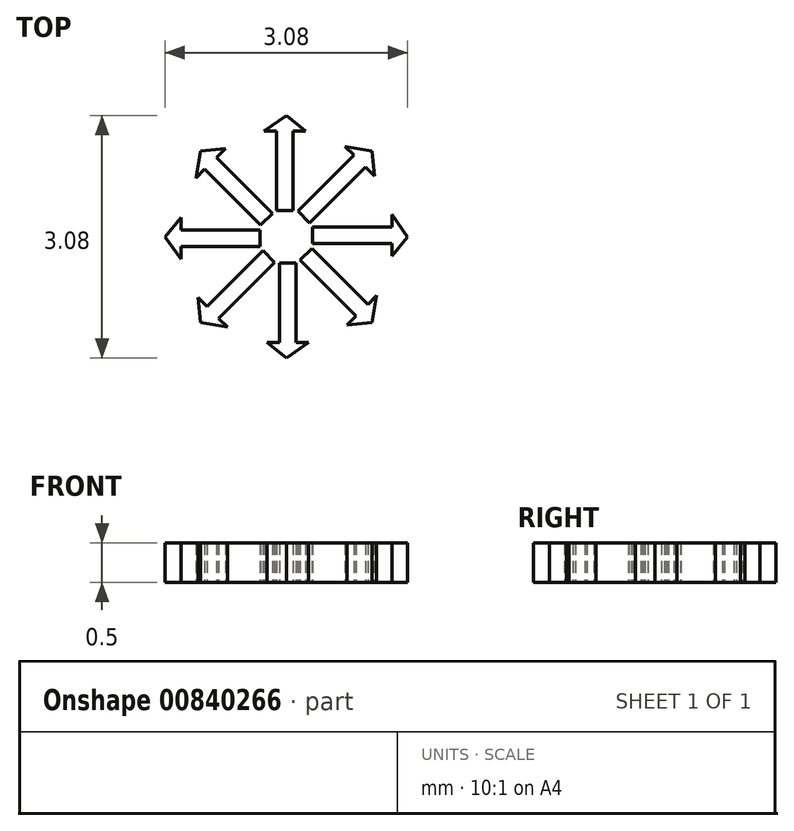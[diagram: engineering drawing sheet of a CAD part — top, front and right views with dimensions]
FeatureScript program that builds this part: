
annotation { "Feature Type Name" : "Feature", "Feature Type Description" : "" }
export const myFeature = defineFeature(function(context is Context, id is Id, definition is map)
    precondition{}
    {
        {
            var Q0;
            Q0=qCreatedBy(makeId("Top.planeOp"),FACE);
            var sketch = newSketch(context, id + "F0", { "sketchPlane" : qUnion([Q0])});
            skLineSegment(sketch, "E0.2.5", {"start": v(-1.34, -0.04) * mm, "end": v(-1.34, -0.15) * mm});
            skLineSegment(sketch, "E0.2.6", {"start": v(-0.34, -0.04) * mm, "end": v(-0.34, 0.04) * mm});
            skLineSegment(sketch, "E0.2.7", {"start": v(-1.34, 0.04) * mm, "end": v(-1.34, 0.15) * mm});
            skLineSegment(sketch, "E0.2.8", {"start": v(-1.34, -0.04) * mm, "end": v(-1.34, 0.04) * mm});
            skLineSegment(sketch, "E1.0", {"start": v(-1.34, 0.09) * mm, "end": v(-0.34, 0.09) * mm});
            skLineSegment(sketch, "E2.0", {"start": v(-1.34, -0.13) * mm, "end": v(-0.34, -0.13) * mm});
            skLineSegment(sketch, "E3", {"start": v(-0.34, 0.09) * mm, "end": v(-0.34, -0.13) * mm});
            skLineSegment(sketch, "E4", {"start": v(-1.34, 0.09) * mm, "end": v(-1.34, 0.25) * mm});
            skLineSegment(sketch, "E5", {"start": v(-1.34, -0.13) * mm, "end": v(-1.34, -0.29) * mm});
            skLineSegment(sketch, "E6", {"start": v(-1.34, 0.25) * mm, "end": v(-1.54, 0) * mm});
            skLineSegment(sketch, "E7", {"start": v(-1.34, -0.29) * mm, "end": v(-1.54, 0) * mm});
            skLineSegment(sketch, "E8.1.0", {"start": v(-1.12, -0.77) * mm, "end": v(-1.09, -1.09) * mm});
            skLineSegment(sketch, "E8.1.1", {"start": v(-1, -0.89) * mm, "end": v(-0.3, -0.18) * mm});
            skLineSegment(sketch, "E8.1.2", {"start": v(-0.75, -1.15) * mm, "end": v(-1.09, -1.09) * mm});
            skLineSegment(sketch, "E8.1.3", {"start": v(-0.86, -1.04) * mm, "end": v(-0.15, -0.33) * mm});
            skLineSegment(sketch, "E8.1.4", {"start": v(-1, -0.89) * mm, "end": v(-1.12, -0.77) * mm});
            skLineSegment(sketch, "E8.1.5", {"start": v(-0.86, -1.04) * mm, "end": v(-0.75, -1.15) * mm});
            skLineSegment(sketch, "E8.1.6", {"start": v(-0.21, -0.26) * mm, "end": v(-0.26, -0.21) * mm});
            skLineSegment(sketch, "E8.1.7", {"start": v(-0.3, -0.18) * mm, "end": v(-0.15, -0.33) * mm});
            skLineSegment(sketch, "E8.1.8", {"start": v(-0.92, -0.97) * mm, "end": v(-0.84, -1.05) * mm});
            skLineSegment(sketch, "E8.1.9", {"start": v(-0.92, -0.97) * mm, "end": v(-0.97, -0.92) * mm});
            skLineSegment(sketch, "E8.1.10", {"start": v(-0.97, -0.92) * mm, "end": v(-1.05, -0.84) * mm});
            skLineSegment(sketch, "E8.2.0", {"start": v(-0.25, -1.34) * mm, "end": v(0, -1.54) * mm});
            skLineSegment(sketch, "E8.2.1", {"start": v(-0.09, -1.34) * mm, "end": v(-0.09, -0.34) * mm});
            skLineSegment(sketch, "E8.2.2", {"start": v(0.29, -1.34) * mm, "end": v(0, -1.54) * mm});
            skLineSegment(sketch, "E8.2.3", {"start": v(0.13, -1.34) * mm, "end": v(0.13, -0.34) * mm});
            skLineSegment(sketch, "E8.2.4", {"start": v(-0.09, -1.34) * mm, "end": v(-0.25, -1.34) * mm});
            skLineSegment(sketch, "E8.2.5", {"start": v(0.13, -1.34) * mm, "end": v(0.29, -1.34) * mm});
            skLineSegment(sketch, "E8.2.6", {"start": v(0.04, -0.34) * mm, "end": v(-0.04, -0.34) * mm});
            skLineSegment(sketch, "E8.2.7", {"start": v(-0.09, -0.34) * mm, "end": v(0.13, -0.34) * mm});
            skLineSegment(sketch, "E8.2.8", {"start": v(0.04, -1.34) * mm, "end": v(0.15, -1.34) * mm});
            skLineSegment(sketch, "E8.2.9", {"start": v(0.04, -1.34) * mm, "end": v(-0.04, -1.34) * mm});
            skLineSegment(sketch, "E8.2.10", {"start": v(-0.04, -1.34) * mm, "end": v(-0.15, -1.34) * mm});
            skPoint(sketch, "E8.center", {"position": v(0, 0) * mm});
            skLineSegment(sketch, "E9.3.3.0", {"start": v(0.89, -1) * mm, "end": v(0.18, -0.3) * mm});
            skLineSegment(sketch, "E9.6.3.0", {"start": v(1.15, -0.75) * mm, "end": v(1.09, -1.09) * mm});
            skLineSegment(sketch, "E9.7.3.0", {"start": v(0.77, -1.12) * mm, "end": v(1.09, -1.09) * mm});
            skLineSegment(sketch, "E9.9.3.0", {"start": v(1.04, -0.86) * mm, "end": v(0.33, -0.15) * mm});
            skLineSegment(sketch, "E9.12.3.0", {"start": v(0.89, -1) * mm, "end": v(0.77, -1.12) * mm});
            skLineSegment(sketch, "E9.15.3.0", {"start": v(1.04, -0.86) * mm, "end": v(1.15, -0.75) * mm});
            skLineSegment(sketch, "E9.18.3.0", {"start": v(0.26, -0.21) * mm, "end": v(0.21, -0.26) * mm});
            skLineSegment(sketch, "E9.21.3.0", {"start": v(0.18, -0.3) * mm, "end": v(0.33, -0.15) * mm});
            skLineSegment(sketch, "E9.24.3.0", {"start": v(0.97, -0.92) * mm, "end": v(1.05, -0.84) * mm});
            skLineSegment(sketch, "E9.27.3.0", {"start": v(0.97, -0.92) * mm, "end": v(0.92, -0.97) * mm});
            skLineSegment(sketch, "E9.30.3.0", {"start": v(0.92, -0.97) * mm, "end": v(0.84, -1.05) * mm});
            skLineSegment(sketch, "E9.3.4.0", {"start": v(1.34, -0.09) * mm, "end": v(0.34, -0.09) * mm});
            skLineSegment(sketch, "E9.6.4.0", {"start": v(1.34, 0.29) * mm, "end": v(1.54, 0) * mm});
            skLineSegment(sketch, "E9.7.4.0", {"start": v(1.34, -0.25) * mm, "end": v(1.54, 0) * mm});
            skLineSegment(sketch, "E9.9.4.0", {"start": v(1.34, 0.13) * mm, "end": v(0.34, 0.13) * mm});
            skLineSegment(sketch, "E9.12.4.0", {"start": v(1.34, -0.09) * mm, "end": v(1.34, -0.25) * mm});
            skLineSegment(sketch, "E9.15.4.0", {"start": v(1.34, 0.13) * mm, "end": v(1.34, 0.29) * mm});
            skLineSegment(sketch, "E9.18.4.0", {"start": v(0.34, 0.04) * mm, "end": v(0.34, -0.04) * mm});
            skLineSegment(sketch, "E9.21.4.0", {"start": v(0.34, -0.09) * mm, "end": v(0.34, 0.13) * mm});
            skLineSegment(sketch, "E9.24.4.0", {"start": v(1.34, 0.04) * mm, "end": v(1.34, 0.15) * mm});
            skLineSegment(sketch, "E9.27.4.0", {"start": v(1.34, 0.04) * mm, "end": v(1.34, -0.04) * mm});
            skLineSegment(sketch, "E9.30.4.0", {"start": v(1.34, -0.04) * mm, "end": v(1.34, -0.15) * mm});
            skLineSegment(sketch, "E9.3.5.0", {"start": v(1, 0.89) * mm, "end": v(0.3, 0.18) * mm});
            skLineSegment(sketch, "E9.6.5.0", {"start": v(0.75, 1.15) * mm, "end": v(1.09, 1.09) * mm});
            skLineSegment(sketch, "E9.7.5.0", {"start": v(1.12, 0.77) * mm, "end": v(1.09, 1.09) * mm});
            skLineSegment(sketch, "E9.9.5.0", {"start": v(0.86, 1.04) * mm, "end": v(0.15, 0.33) * mm});
            skLineSegment(sketch, "E9.12.5.0", {"start": v(1, 0.89) * mm, "end": v(1.12, 0.77) * mm});
            skLineSegment(sketch, "E9.15.5.0", {"start": v(0.86, 1.04) * mm, "end": v(0.75, 1.15) * mm});
            skLineSegment(sketch, "E9.18.5.0", {"start": v(0.21, 0.26) * mm, "end": v(0.26, 0.21) * mm});
            skLineSegment(sketch, "E9.21.5.0", {"start": v(0.3, 0.18) * mm, "end": v(0.15, 0.33) * mm});
            skLineSegment(sketch, "E9.24.5.0", {"start": v(0.92, 0.97) * mm, "end": v(0.84, 1.05) * mm});
            skLineSegment(sketch, "E9.27.5.0", {"start": v(0.92, 0.97) * mm, "end": v(0.97, 0.92) * mm});
            skLineSegment(sketch, "E9.30.5.0", {"start": v(0.97, 0.92) * mm, "end": v(1.05, 0.84) * mm});
            skLineSegment(sketch, "E9.3.6.0", {"start": v(0.09, 1.34) * mm, "end": v(0.09, 0.34) * mm});
            skLineSegment(sketch, "E9.6.6.0", {"start": v(-0.29, 1.34) * mm, "end": v(0, 1.54) * mm});
            skLineSegment(sketch, "E9.7.6.0", {"start": v(0.25, 1.34) * mm, "end": v(0, 1.54) * mm});
            skLineSegment(sketch, "E9.9.6.0", {"start": v(-0.13, 1.34) * mm, "end": v(-0.13, 0.34) * mm});
            skLineSegment(sketch, "E9.12.6.0", {"start": v(0.09, 1.34) * mm, "end": v(0.25, 1.34) * mm});
            skLineSegment(sketch, "E9.15.6.0", {"start": v(-0.13, 1.34) * mm, "end": v(-0.29, 1.34) * mm});
            skLineSegment(sketch, "E9.18.6.0", {"start": v(-0.04, 0.34) * mm, "end": v(0.04, 0.34) * mm});
            skLineSegment(sketch, "E9.21.6.0", {"start": v(0.09, 0.34) * mm, "end": v(-0.13, 0.34) * mm});
            skLineSegment(sketch, "E9.24.6.0", {"start": v(-0.04, 1.34) * mm, "end": v(-0.15, 1.34) * mm});
            skLineSegment(sketch, "E9.27.6.0", {"start": v(-0.04, 1.34) * mm, "end": v(0.04, 1.34) * mm});
            skLineSegment(sketch, "E9.30.6.0", {"start": v(0.04, 1.34) * mm, "end": v(0.15, 1.34) * mm});
            skLineSegment(sketch, "E9.3.7.0", {"start": v(-0.89, 1) * mm, "end": v(-0.18, 0.3) * mm});
            skLineSegment(sketch, "E9.6.7.0", {"start": v(-1.15, 0.75) * mm, "end": v(-1.09, 1.09) * mm});
            skLineSegment(sketch, "E9.7.7.0", {"start": v(-0.77, 1.12) * mm, "end": v(-1.09, 1.09) * mm});
            skLineSegment(sketch, "E9.9.7.0", {"start": v(-1.04, 0.86) * mm, "end": v(-0.33, 0.15) * mm});
            skLineSegment(sketch, "E9.12.7.0", {"start": v(-0.89, 1) * mm, "end": v(-0.77, 1.12) * mm});
            skLineSegment(sketch, "E9.15.7.0", {"start": v(-1.04, 0.86) * mm, "end": v(-1.15, 0.75) * mm});
            skLineSegment(sketch, "E9.18.7.0", {"start": v(-0.26, 0.21) * mm, "end": v(-0.21, 0.26) * mm});
            skLineSegment(sketch, "E9.21.7.0", {"start": v(-0.18, 0.3) * mm, "end": v(-0.33, 0.15) * mm});
            skLineSegment(sketch, "E9.24.7.0", {"start": v(-0.97, 0.92) * mm, "end": v(-1.05, 0.84) * mm});
            skLineSegment(sketch, "E9.27.7.0", {"start": v(-0.97, 0.92) * mm, "end": v(-0.92, 0.97) * mm});
            skLineSegment(sketch, "E9.30.7.0", {"start": v(-0.92, 0.97) * mm, "end": v(-0.84, 1.05) * mm});
            skSolve(sketch);
        }
        {
            var Q0;
            Q0=makeQuery(id+"F0.imprint","IMPRINT",FACE,{"disambiguationData":[TD([[makeQuery(id+"F0.imprint","IMPRINT",EDGE,{"derivedFrom":sQuery(id+"F0.wireOp",EDGE,"E0.5.1")}),-1.0]])]});
            var Q1;
            Q1=makeQuery(id+"F0.imprint","IMPRINT",FACE,{"disambiguationData":[TD([[makeQuery(id+"F0.imprint","IMPRINT",EDGE,{"derivedFrom":sQuery(id+"F0.wireOp",EDGE,"E0.1.0")}),-1.0]])]});
            var Q2;
            Q2=makeQuery(id+"F0.imprint","IMPRINT",FACE,{"disambiguationData":[TD([[makeQuery(id+"F0.imprint","IMPRINT",EDGE,{"derivedFrom":sQuery(id+"F0.wireOp",EDGE,"E0.3.1")}),-1.0]])]});
            var Q3;
            Q3=makeQuery(id+"F0.imprint","IMPRINT",FACE,{"disambiguationData":[TD([[makeQuery(id+"F0.imprint","IMPRINT",EDGE,{"derivedFrom":sQuery(id+"F0.wireOp",EDGE,"E0.4.0")}),-1.0]])]});
            var Q4;
            Q4=makeQuery(id+"F0.imprint","IMPRINT",FACE,{"disambiguationData":[TD([[makeQuery(id+"F0.imprint","IMPRINT",EDGE,{"derivedFrom":sQuery(id+"F0.wireOp",EDGE,"E0.2.1")}),-1.0]])]});
            var Q5;
            Q5=makeQuery(id+"F0.imprint","IMPRINT",FACE,{"disambiguationData":[TD([[makeQuery(id+"F0.imprint","IMPRINT",EDGE,{"derivedFrom":sQuery(id+"F0.wireOp",EDGE,"E0.5.0")}),-1.0]])]});
            var Q6;
            Q6=makeQuery(id+"F0.imprint","IMPRINT",FACE,{"disambiguationData":[TD([[makeQuery(id+"F0.imprint","IMPRINT",EDGE,{"derivedFrom":sQuery(id+"F0.wireOp",EDGE,"E0.1.1")}),-1.0]])]});
            var Q7;
            Q7=makeQuery(id+"F0.imprint","IMPRINT",FACE,{"disambiguationData":[TD([[makeQuery(id+"F0.imprint","IMPRINT",EDGE,{"derivedFrom":sQuery(id+"F0.wireOp",EDGE,"E0.4.1")}),-1.0]])]});
            var Q8;
            Q8=makeQuery(id+"F0.imprint","IMPRINT",FACE,{"disambiguationData":[TD([[makeQuery(id+"F0.imprint","IMPRINT",EDGE,{"derivedFrom":sQuery(id+"F0.wireOp",EDGE,"E0.2.0")}),-1.0]])]});
            var Q9;
            Q9=makeQuery(id+"F0.imprint","IMPRINT",FACE,{"disambiguationData":[TD([[makeQuery(id+"F0.imprint","IMPRINT",EDGE,{"derivedFrom":sQuery(id+"F0.wireOp",EDGE,"EAGoIer3-Kxh2-T1gJ-fZua-uYb5fhu8yMPO")}),1.0]])]});
            var Q10;
            Q10=makeQuery(id+"F0.imprint","IMPRINT",FACE,{"disambiguationData":[TD([[makeQuery(id+"F0.imprint","IMPRINT",EDGE,{"derivedFrom":sQuery(id+"F0.wireOp",EDGE,"E0.3.0")}),-1.0]])]});
            var Q11;
            Q11=makeQuery(id+"F0.imprint","IMPRINT",FACE,{"disambiguationData":[TD([[makeQuery(id+"F0.imprint","IMPRINT",EDGE,{"derivedFrom":sQuery(id+"F0.wireOp",EDGE,"6h74pHwc-frKd-KBCy-3KOA-2A4SLII55MS7")}),1.0]])]});
            var Q12;
            Q12=makeQuery(id+"F0.imprint","IMPRINT",FACE,{"disambiguationData":[TD([[makeQuery(id+"F0.imprint","IMPRINT",EDGE,{"derivedFrom":sQuery(id+"F0.wireOp",EDGE,"c3a0d5a2-d673-4ad7-92ee-11ab09311ead.6.7.0")}),1.0]])]});
            var Q13;
            Q13=makeQuery(id+"F0.imprint","IMPRINT",FACE,{"disambiguationData":[TD([[makeQuery(id+"F0.imprint","IMPRINT",EDGE,{"derivedFrom":sQuery(id+"F0.wireOp",EDGE,"c3a0d5a2-d673-4ad7-92ee-11ab09311ead.3.6.0")}),-1.0]])]});
            var Q14;
            Q14=makeQuery(id+"F0.imprint","IMPRINT",FACE,{"disambiguationData":[TD([[makeQuery(id+"F0.imprint","IMPRINT",EDGE,{"derivedFrom":sQuery(id+"F0.wireOp",EDGE,"c3a0d5a2-d673-4ad7-92ee-11ab09311ead.3.7.0")}),-1.0]])]});
            var Q15;
            Q15=makeQuery(id+"F0.imprint","IMPRINT",FACE,{"disambiguationData":[TD([[makeQuery(id+"F0.imprint","IMPRINT",EDGE,{"derivedFrom":sQuery(id+"F0.wireOp",EDGE,"c3a0d5a2-d673-4ad7-92ee-11ab09311ead.6.6.0")}),1.0]])]});
            var Q16;
            {var subQ2=sQuery(id+"F0.wireOp",EDGE,"E0.2.6");Q16=makeQuery(id+"F0.imprint","IMPRINT",FACE,{"disambiguationData":[TD([[makeQuery(id+"F0.imprint","IMPRINT",EDGE,{"derivedFrom":subQ2}),1.0]])]});}
            var Q17;
            {var subQ2=sQuery(id+"F0.wireOp",EDGE,"E0.2.8");Q17=makeQuery(id+"F0.imprint","IMPRINT",FACE,{"disambiguationData":[TD([[makeQuery(id+"F0.imprint","IMPRINT",EDGE,{"derivedFrom":subQ2}),1.0]])]});}
            var Q18;
            {var subQ3=sQuery(id+"F0.wireOp",EDGE,"E9.3.7.0");Q18=makeQuery(id+"F0.imprint","IMPRINT",FACE,{"disambiguationData":[TD([[makeQuery(id+"F0.imprint","IMPRINT",EDGE,{"derivedFrom":subQ3}),-1.0]])]});}
            var Q19;
            {var subQ4=sQuery(id+"F0.wireOp",EDGE,"E9.6.7.0");Q19=makeQuery(id+"F0.imprint","IMPRINT",FACE,{"disambiguationData":[TD([[makeQuery(id+"F0.imprint","IMPRINT",EDGE,{"derivedFrom":subQ4}),-1.0]])]});}
            var Q20;
            {var subQ4=sQuery(id+"F0.wireOp",EDGE,"E9.6.6.0");Q20=makeQuery(id+"F0.imprint","IMPRINT",FACE,{"disambiguationData":[TD([[makeQuery(id+"F0.imprint","IMPRINT",EDGE,{"derivedFrom":subQ4}),-1.0]])]});}
            var Q21;
            {var subQ3=sQuery(id+"F0.wireOp",EDGE,"E9.3.6.0");Q21=makeQuery(id+"F0.imprint","IMPRINT",FACE,{"disambiguationData":[TD([[makeQuery(id+"F0.imprint","IMPRINT",EDGE,{"derivedFrom":subQ3}),-1.0]])]});}
            var Q22;
            {var subQ3=sQuery(id+"F0.wireOp",EDGE,"E9.3.5.0");Q22=makeQuery(id+"F0.imprint","IMPRINT",FACE,{"disambiguationData":[TD([[makeQuery(id+"F0.imprint","IMPRINT",EDGE,{"derivedFrom":subQ3}),-1.0]])]});}
            var Q23;
            {var subQ4=sQuery(id+"F0.wireOp",EDGE,"E9.6.5.0");Q23=makeQuery(id+"F0.imprint","IMPRINT",FACE,{"disambiguationData":[TD([[makeQuery(id+"F0.imprint","IMPRINT",EDGE,{"derivedFrom":subQ4}),-1.0]])]});}
            var Q24;
            {var subQ4=sQuery(id+"F0.wireOp",EDGE,"E9.6.4.0");Q24=makeQuery(id+"F0.imprint","IMPRINT",FACE,{"disambiguationData":[TD([[makeQuery(id+"F0.imprint","IMPRINT",EDGE,{"derivedFrom":subQ4}),-1.0]])]});}
            var Q25;
            {var subQ3=sQuery(id+"F0.wireOp",EDGE,"E9.3.4.0");Q25=makeQuery(id+"F0.imprint","IMPRINT",FACE,{"disambiguationData":[TD([[makeQuery(id+"F0.imprint","IMPRINT",EDGE,{"derivedFrom":subQ3}),-1.0]])]});}
            var Q26;
            {var subQ3=sQuery(id+"F0.wireOp",EDGE,"E9.3.3.0");Q26=makeQuery(id+"F0.imprint","IMPRINT",FACE,{"disambiguationData":[TD([[makeQuery(id+"F0.imprint","IMPRINT",EDGE,{"derivedFrom":subQ3}),-1.0]])]});}
            var Q27;
            {var subQ4=sQuery(id+"F0.wireOp",EDGE,"E9.6.3.0");Q27=makeQuery(id+"F0.imprint","IMPRINT",FACE,{"disambiguationData":[TD([[makeQuery(id+"F0.imprint","IMPRINT",EDGE,{"derivedFrom":subQ4}),-1.0]])]});}
            var Q28;
            {var subQ3=sQuery(id+"F0.wireOp",EDGE,"E8.2.1");Q28=makeQuery(id+"F0.imprint","IMPRINT",FACE,{"disambiguationData":[TD([[makeQuery(id+"F0.imprint","IMPRINT",EDGE,{"derivedFrom":subQ3}),-1.0]])]});}
            var Q29;
            {var subQ1=sQuery(id+"F0.wireOp",EDGE,"E8.2.0");Q29=makeQuery(id+"F0.imprint","IMPRINT",FACE,{"disambiguationData":[TD([[makeQuery(id+"F0.imprint","IMPRINT",EDGE,{"derivedFrom":subQ1}),1.0]])]});}
            var Q30;
            {var subQ1=sQuery(id+"F0.wireOp",EDGE,"E8.1.0");Q30=makeQuery(id+"F0.imprint","IMPRINT",FACE,{"disambiguationData":[TD([[makeQuery(id+"F0.imprint","IMPRINT",EDGE,{"derivedFrom":subQ1}),1.0]])]});}
            var Q31;
            {var subQ3=sQuery(id+"F0.wireOp",EDGE,"E8.1.1");Q31=makeQuery(id+"F0.imprint","IMPRINT",FACE,{"disambiguationData":[TD([[makeQuery(id+"F0.imprint","IMPRINT",EDGE,{"derivedFrom":subQ3}),-1.0]])]});}
            extrude(context, id + "F1", {"entities" : qUnion([Q0, Q1, Q2, Q3, Q4, Q5, Q6, Q7, Q8, Q9, Q10, Q11, Q12, Q13, Q14, Q15, Q16, Q17, Q18, Q19, Q20, Q21, Q22, Q23, Q24, Q25, Q26, Q27, Q28, Q29, Q30, Q31]), "depth" : .5 * mm, "offsetDistance" : 25 * mm});
        }
    });
